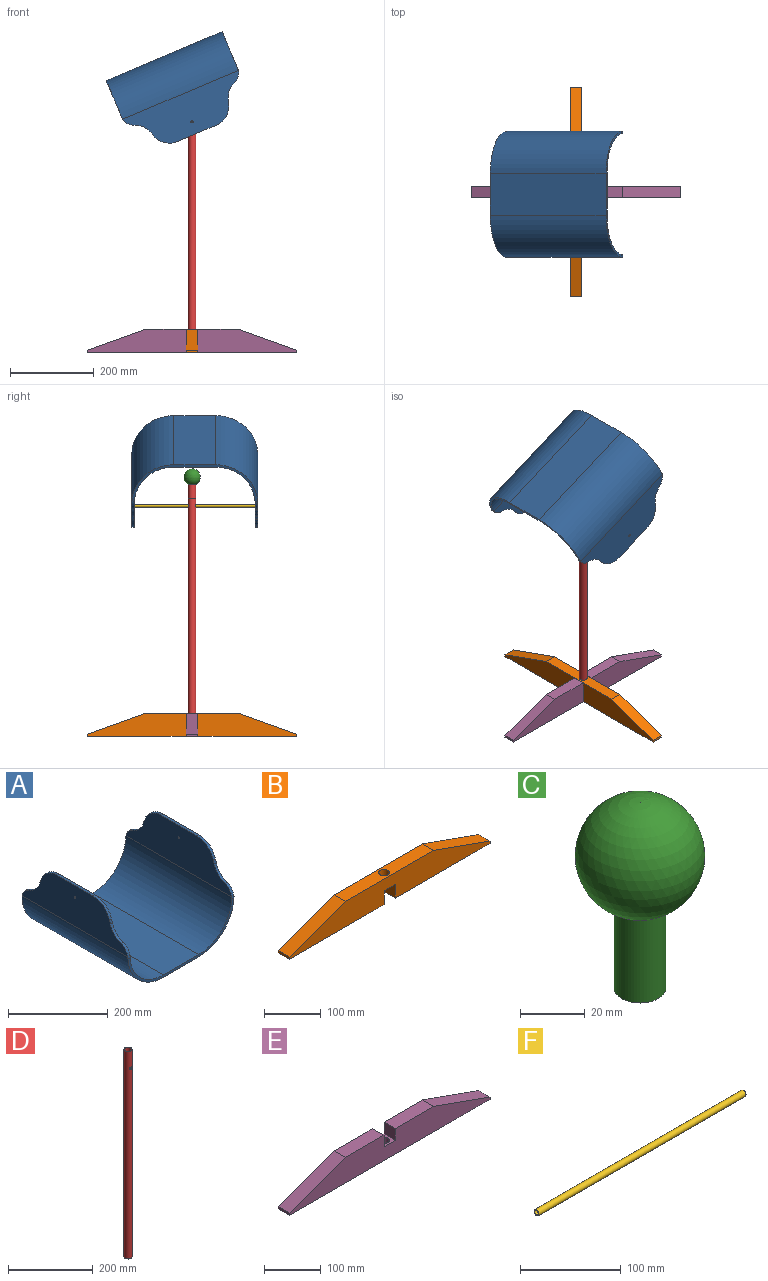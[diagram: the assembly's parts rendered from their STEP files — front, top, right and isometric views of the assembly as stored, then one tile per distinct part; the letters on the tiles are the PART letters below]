
ASSEMBLY  parts=6 mates=5
PART A: 32 faces, bbox 300x300x200 mm
  f0: plane 299.17x100mm, normal (1,0,0), area 21568.5mm2, adj f1,f2,f8,f9,f10,f11,f13,f14
  f1: cylinder r=100mm len=300mm, axis (0,1,0), area 47122.5mm2, adj f0,f6,f7,f11,f12,f16
  f2: plane 99.25x6mm, normal (0,0,1), area 595.5mm2, adj f0,f3,f9,f14
  f3: plane 299.17x100mm, normal (-1,0,0), area 21568.5mm2, adj f2,f4,f8,f9,f10,f11,f13,f14
  f4: cylinder r=94mm len=300mm, axis (0,1,0), area 44295.1mm2, adj f3,f5,f7,f11,f12,f16
  f5: plane 300x100mm, normal (0,0,1), area 30000mm2, adj f4,f7,f12,f21
  f6: plane 300x100mm, normal (0,0,-1), area 30000mm2, adj f1,f7,f12,f18
  f7: plane 299.75x95.01mm, normal (0,1,0), area 2368.6mm2, adj f1,f4,f5,f6,f11,f18,f21,f25
  f8: plane 7.07x6mm, normal (0,0.96,0.27), area 44.1mm2, adj f0,f3,f9,f10
  f9: cylinder r=50mm len=48.13mm, axis (-1,0,0), area 389mm2, adj f0,f2,f3,f8
  f10: cylinder r=50mm len=33.33mm, axis (-1,0,0), area 282.2mm2, adj f0,f3,f8,f11
  f11: cylinder r=30mm len=28.12mm, axis (-1,0,0), area 218.7mm2, adj f0,f1,f3,f4,f7,f10
  f12: plane 299.75x95.01mm, normal (0,-1,0), area 2368.6mm2, adj f1,f4,f5,f6,f16,f18,f21,f29
  f13: plane 7.07x6mm, normal (0,-0.96,0.27), area 44.1mm2, adj f0,f3,f14,f15
  f14: cylinder r=50mm len=48.13mm, axis (-1,0,0), area 389mm2, adj f0,f2,f3,f13
  f15: cylinder r=50mm len=33.33mm, axis (-1,0,0), area 282.2mm2, adj f0,f3,f13,f16
  f16: cylinder r=30mm len=28.12mm, axis (-1,0,0), area 218.7mm2, adj f0,f1,f3,f4,f12,f15
  f17: plane 299.17x100mm, normal (-1,0,0), area 21568.5mm2, adj f18,f19,f22,f23,f24,f25,f26,f27
  f18: cylinder r=100mm len=300mm, axis (0,1,0), area 47122.5mm2, adj f6,f7,f12,f17,f25,f29
  f19: plane 99.25x6mm, normal (0,0,1), area 595.5mm2, adj f17,f20,f23,f27
  f20: plane 299.17x100mm, normal (1,0,0), area 21568.5mm2, adj f19,f21,f22,f23,f24,f25,f26,f27
  f21: cylinder r=94mm len=300mm, axis (0,1,0), area 44295.1mm2, adj f5,f7,f12,f20,f25,f29
  f22: plane 7.07x6mm, normal (0,0.96,0.27), area 44.1mm2, adj f17,f20,f23,f24
  f23: cylinder r=50mm len=48.13mm, axis (1,0,0), area 389mm2, adj f17,f19,f20,f22
  f24: cylinder r=50mm len=33.33mm, axis (1,0,0), area 282.2mm2, adj f17,f20,f22,f25
  f25: cylinder r=30mm len=28.12mm, axis (1,0,0), area 218.7mm2, adj f7,f17,f18,f20,f21,f24
  f26: plane 7.07x6mm, normal (0,-0.96,0.27), area 44.1mm2, adj f17,f20,f27,f28
  f27: cylinder r=50mm len=48.13mm, axis (1,0,0), area 389mm2, adj f17,f19,f20,f26
  f28: cylinder r=50mm len=33.33mm, axis (1,0,0), area 282.2mm2, adj f17,f20,f26,f29
  f29: cylinder r=30mm len=28.12mm, axis (1,0,0), area 218.7mm2, adj f12,f17,f18,f20,f21,f28
  f30: cylinder r=2.5mm len=6mm, axis (1,0,0), area 94.2mm2, adj f17,f20
  f31: cylinder r=2.5mm len=6mm, axis (1,0,0), area 94.2mm2, adj f0,f3
PART B: 13 faces, bbox 500x28x55 mm
  f0: plane 28x5mm, normal (-1,0,0), area 140mm2, adj f1,f9,f10,f11
  f1: plane 236x28mm, normal (0,0,-1), area 6608mm2, adj f0,f2,f10,f11
  f2: plane 30x28mm, normal (1,0,0), area 840mm2, adj f1,f3,f10,f11
  f3: plane 28x28mm, normal (0,0,-1), area 500.5mm2, adj f2,f4,f10,f11,f12
  f4: plane 30x28mm, normal (-1,0,0), area 840mm2, adj f3,f5,f10,f11
  f5: plane 236x28mm, normal (0,0,-1), area 6608mm2, adj f4,f6,f10,f11
  f6: plane 28x5mm, normal (1,0,0), area 140mm2, adj f5,f7,f10,f11
  f7: plane 140x50mm, normal (0.34,0,0.94), area 4162.5mm2, adj f6,f8,f10,f11
  f8: plane 220x28mm, normal (0,0,1), area 5876.5mm2, adj f7,f9,f10,f11,f12
  f9: plane 140x50mm, normal (-0.34,0,0.94), area 4162.5mm2, adj f0,f8,f10,f11
  f10: plane 500x55mm, normal (0,-1,0), area 19660mm2, adj f0,f1,f2,f3,f4,f5,f6,f7
  f11: plane 500x55mm, normal (0,1,0), area 19660mm2, adj f0,f1,f2,f3,f4,f5,f6,f7
  f12: cylinder r=9.5mm len=25mm, axis (0,0,-1), area 1492.3mm2, adj f3,f8
PART C: 3 faces, bbox 40x40x70 mm
  f0: cylinder r=8mm len=31.67mm, axis (0,0,1), area 1591.9mm2, adj f1,f2
  f1: sphere r=20mm, area 4816.7mm2, adj f0
  f2: plane 16x16mm, normal (0,0,-1), area 201.1mm2, adj f0
PART D: 6 faces, bbox 19x19x600 mm
  f0: cylinder r=8.5mm len=600mm, axis (0,0,-1), area 31965.7mm2, adj f2,f3,f4,f5
  f1: cylinder r=9.5mm len=600mm, axis (0,0,-1), area 35735.9mm2, adj f2,f3,f4,f5
  f2: plane 19x19mm, normal (0,0,1), area 56.5mm2, adj f0,f1
  f3: plane 19x19mm, normal (0,0,-1), area 56.5mm2, adj f0,f1
  f4: cylinder r=3.5mm len=7mm, axis (0,-1,0), area 22.9mm2, adj f0,f1
  f5: cylinder r=3.5mm len=7mm, axis (0,-1,0), area 22.9mm2, adj f0,f1
PART E: 13 faces, bbox 500x28x55 mm
  f0: plane 500x28mm, normal (0,0,-1), area 13716.5mm2, adj f1,f9,f10,f11,f12
  f1: plane 28x5mm, normal (1,0,0), area 140mm2, adj f0,f2,f10,f11
  f2: plane 140x50mm, normal (0.34,0,0.94), area 4162.5mm2, adj f1,f3,f10,f11
  f3: plane 96x28mm, normal (0,0,1), area 2688mm2, adj f2,f4,f10,f11
  f4: plane 28x25mm, normal (-1,0,0), area 700mm2, adj f3,f5,f10,f11
  f5: plane 28x28mm, normal (0,0,1), area 500.5mm2, adj f4,f6,f10,f11,f12
  f6: plane 28x25mm, normal (1,0,0), area 700mm2, adj f5,f7,f10,f11
  f7: plane 96x28mm, normal (0,0,1), area 2688mm2, adj f6,f8,f10,f11
  f8: plane 140x50mm, normal (-0.34,0,0.94), area 4162.5mm2, adj f7,f9,f10,f11
  f9: plane 28x5mm, normal (-1,0,0), area 140mm2, adj f0,f8,f10,f11
  f10: plane 500x55mm, normal (0,-1,0), area 19800mm2, adj f0,f1,f2,f3,f4,f5,f6,f7
  f11: plane 500x55mm, normal (0,1,0), area 19800mm2, adj f0,f1,f2,f3,f4,f5,f6,f7
  f12: cylinder r=9.5mm len=30mm, axis (0,0,1), area 1790.7mm2, adj f0,f5
PART F: 4 faces, bbox 290x7x7 mm
  f0: cylinder r=2.5mm len=290mm, axis (-1,0,0), area 4555.3mm2, adj f2,f3
  f1: cylinder r=3.5mm len=290mm, axis (-1,0,0), area 6377.4mm2, adj f2,f3
  f2: plane 7x7mm, normal (1,0,0), area 18.8mm2, adj f0,f1
  f3: plane 7x7mm, normal (-1,0,0), area 18.8mm2, adj f0,f1
PLACE A rot(axis=(0.7,0.7,0.14),163.8deg) t=(202.49,32.42,682.74)mm
PLACE B rot(axis=(0,0,1),90deg) t=(116.75,-211.06,-82.33)mm
PLACE C t=(130.75,38.94,536)mm
PLACE D t=(130.75,38.94,-82.33)mm
PLACE E t=(-119.25,52.94,-82.33)mm fixed
PLACE F rot(axis=(0.64,0.64,0.41),135.3deg) t=(130.75,31.42,467.67)mm
MATE revolute D.f0 <-> E.f12  axis (0,0,-1) through (130.75,38.94,-82.33)mm
MATE revolute F.f0 <-> A.f30  axis (0,-1,0) through (130.75,176.42,467.67)mm
MATE revolute E.f12 <-> B.f12  axis (0,0,1) through (130.75,38.94,-52.33)mm
MATE revolute C.f0 <-> D.f0  axis (0,0,1) through (130.75,38.94,517.67)mm
MATE revolute A.f30 <-> D.f4  axis (0,1,0) through (130.75,-111.58,467.67)mm
